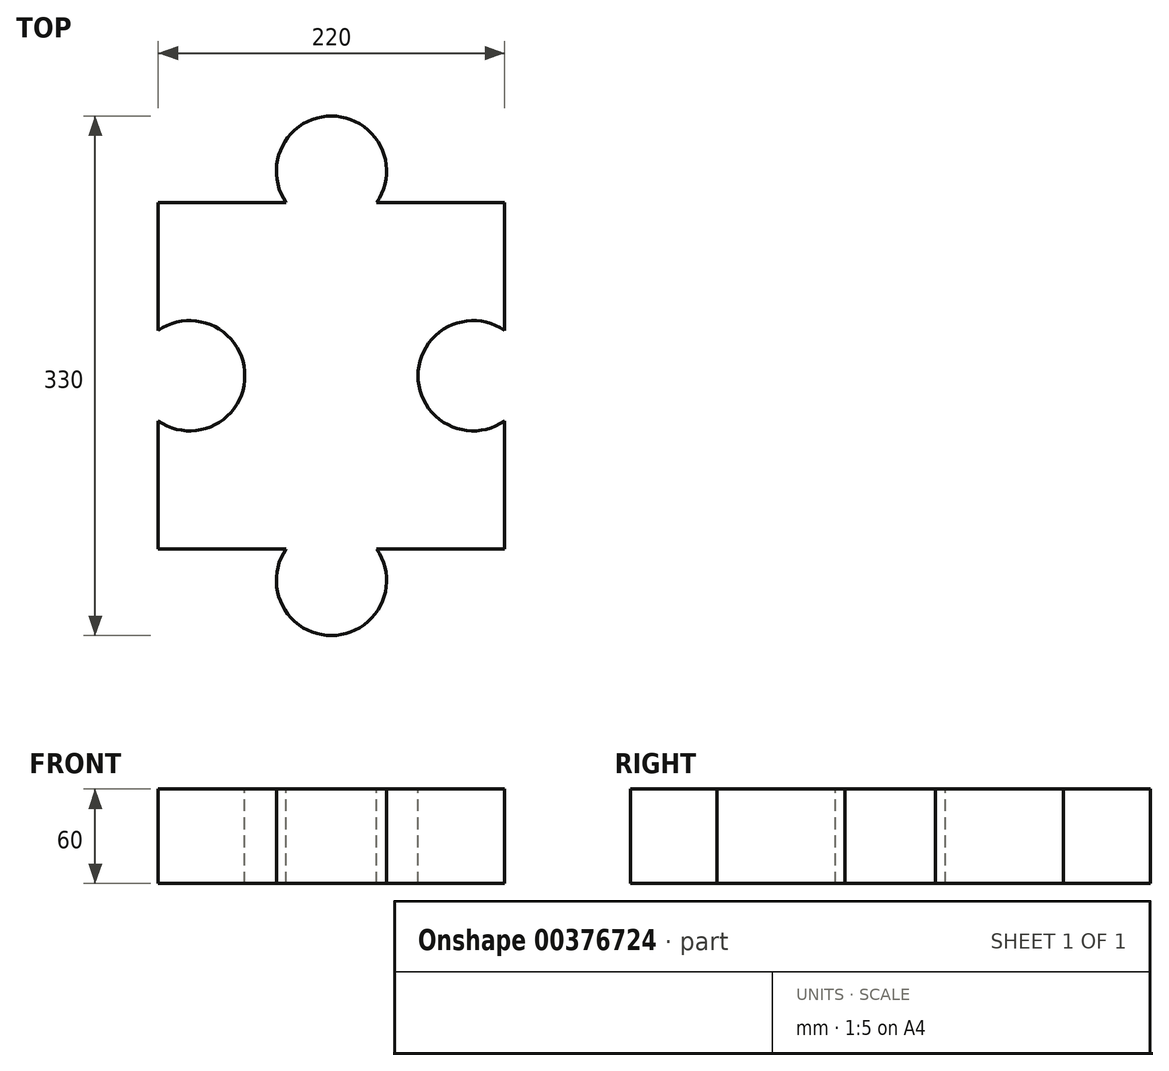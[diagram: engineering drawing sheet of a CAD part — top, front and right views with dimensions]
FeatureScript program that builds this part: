
annotation { "Feature Type Name" : "Feature", "Feature Type Description" : "" }
export const myFeature = defineFeature(function(context is Context, id is Id, definition is map)
    precondition{}
    {
        {
            var Q0;
            Q0=qCreatedBy(makeId("Top.planeOp"),FACE);
            var sketch = newSketch(context, id + "F0", { "sketchPlane" : qUnion([Q0])});
            skLineSegment(sketch, "E0.bottom", {"start": v(110, 165) * mm, "end": v(-110, 165) * mm});
            skLineSegment(sketch, "E0.top", {"start": v(110, -165) * mm, "end": v(-110, -165) * mm});
            skLineSegment(sketch, "E0.left", {"start": v(110, 165) * mm, "end": v(110, -165) * mm});
            skLineSegment(sketch, "E0.right", {"start": v(-110, 165) * mm, "end": v(-110, -165) * mm});
            skPoint(sketch, "E0.middle", {"position": v(0, 0) * mm});
            skSolve(sketch);
        }
        {
            var Q0;
            Q0 = qSketchRegion(id + "F0", true);
            extrude(context, id + "F1", {"entities" : qUnion([Q0]), "depth" : 60 * mm});
        }
        {
            var Q0;
            Q0=makeQuery(id+"F1.opExtrude","CAP_FACE",FACE,{"disambiguationData":[OSD([sQuery(id+"F0.wireOp",EDGE,"E0.bottom"),sQuery(id+"F0.wireOp",EDGE,"E0.top"),sQuery(id+"F0.wireOp",EDGE,"E0.left"),sQuery(id+"F0.wireOp",EDGE,"E0.right")])],"isStart":false});
            var sketch = newSketch(context, id + "F2", { "sketchPlane" : qUnion([Q0])});
            skArc(sketch, "E1", {"start": v(28.72, 110) * mm, "mid": v(0, 165) * mm, "end": v(-28.72, 110) * mm});
            skLineSegment(sketch, "E2", {"start": v(-110, 165) * mm, "end": v(-110, 110) * mm});
            skLineSegment(sketch, "E3", {"start": v(-110, 110) * mm, "end": v(-28.72, 110) * mm});
            skLineSegment(sketch, "E4", {"start": v(-110, 165) * mm, "end": v(110, 165) * mm});
            skLineSegment(sketch, "E5", {"start": v(110, 165) * mm, "end": v(110, 110) * mm});
            skLineSegment(sketch, "E6", {"start": v(110, 110) * mm, "end": v(28.72, 110) * mm});
            skLineSegment(sketch, "E7.MirrorCS", {"start": v(110, -110) * mm, "end": v(28.72, -110) * mm});
            skLineSegment(sketch, "E8.MirrorCS", {"start": v(110, -165) * mm, "end": v(110, -110) * mm});
            skLineSegment(sketch, "E9.MirrorCS", {"start": v(-110, -165) * mm, "end": v(110, -165) * mm});
            skLineSegment(sketch, "E10.MirrorCS", {"start": v(-110, -110) * mm, "end": v(-28.72, -110) * mm});
            skArc(sketch, "E11.MirrorCS", {"start": v(28.72, -110) * mm, "mid": v(0, -165) * mm, "end": v(-28.72, -110) * mm});
            skLineSegment(sketch, "E12.MirrorCS", {"start": v(-110, -165) * mm, "end": v(-110, -110) * mm});
            skSolve(sketch);
        }
        {
            var Q0;
            Q0 = qSketchRegion(id + "F2", true);
            extrude(context, id + "F3", {"entities" : qUnion([Q0]), "operationType" : NewBodyOperationType.REMOVE, "endBound" : BoundingType.THROUGH_ALL, "oppositeDirection" : true, "depth" : 25 * mm});
        }
        {
            var Q0;
            Q0=makeQuery(id+"F1.opExtrude","CAP_FACE",FACE,{"disambiguationData":[OSD([sQuery(id+"F0.wireOp",EDGE,"E0.bottom"),sQuery(id+"F0.wireOp",EDGE,"E0.top"),sQuery(id+"F0.wireOp",EDGE,"E0.left"),sQuery(id+"F0.wireOp",EDGE,"E0.right")])],"isStart":false});
            var sketch = newSketch(context, id + "F4", { "sketchPlane" : qUnion([Q0])});
            skCircle(sketch, "E13", {"center": v(-90, 0) * mm, "radius": 35 * mm});
            skCircle(sketch, "E14.MirrorC", {"center": v(90, 0) * mm, "radius": 35 * mm});
            skSolve(sketch);
        }
        {
            var Q0;
            Q0 = qSketchRegion(id + "F4", true);
            extrude(context, id + "F5", {"entities" : qUnion([Q0]), "operationType" : NewBodyOperationType.REMOVE, "endBound" : BoundingType.THROUGH_ALL, "oppositeDirection" : true, "depth" : 25 * mm});
        }
    });
